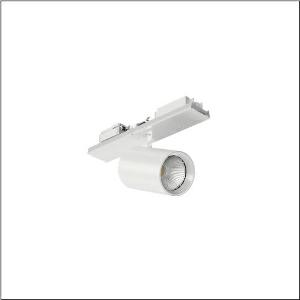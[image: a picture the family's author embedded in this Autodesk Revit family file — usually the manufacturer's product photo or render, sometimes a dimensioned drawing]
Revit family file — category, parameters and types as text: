
# Revit family: licross_r__spot_31_51sl147a43b_2678
name_source: partatom
category: Lighting Fixtures
units: mm (PartAtom-declared; Revit-internal decimal feet)

## family parameters
Cut with Voids When Loaded = No
Host = Face
Light Source = No
Part Type = Normal
Room Calculation Point = No
Round Connector Dimension = Use Diameter
Shared = No

## types (1)
- --- (1 x LED, 3720 lm, 27.9 W, 4000K)
    Apparent Load = 28 VA
    CIE Flux Codes = 93 97 100 100 100
    Color Rendering = 90
    Color Temperature = 4000K
    Default Elevation = 1800 mm
    Description = Licross® Spot 31, directional spotlight, light control with lens, of plastic, LED rated luminous flux: 3.720lm, light colour: 940, with plug, 3-pole, with phase selection, mains connection: 220..240V, AC, 50/60Hz, of aluminium, traffic white (RAL 9016), length: 300mm, diameter: 90mm, protection rating (complete): IP20, insulation class (complete): insulation class I (protective earthing), certification: CE, packaging unit: 1 piece
    Height = 175 mm
    Lamp = 1 x LED
    Lamp Light Flux = 3720 lm
    Lamp Power = 27.9 W
    Lamp count = 1
    Length = 90 mm
    Luminous efficacy = 133 lm/W
    Manufacturer = Siteco
    ModVariant = No
    Model = 51SL147A43B
    Mounting Place = Ceiling
    Mounting Type = Pendant
    Number of Poles = 1
    OnlyDefault = Yes
    Power Factor = 1
    Product Name = Licross® Spot 31
    Product group = directional spotlight
    ProductGroupID = 905
    Protection Class = Protection class I
    Protection Degree = IP 20
    RLX_Detail_Level = 1
    RLX_Emergency_Light_Flux = 0 lm
    RLX_Emergency_Type = 0
    RLX_Emergency_Type_DB = No
    RlxData = <blob elided: 14849 chars, md5=414b134d>
    Socket = socket
    Standby Power = 0 W
    System Light Flux = 3720 lm
    System Power = 28 W
    Type Comments = factory setting: luminous flux: 100 % | (ON | ON | ON) | 700 mA
    Type Image = l_1245720.jpg
    URL = http://relux.com
    VarID = @adj_102243
    Voltage = 0 V
    Weight = 0.00 kg
    Width = 0 mm  [stored 0 ft]

note: [stored X ft] marks values corroborated as IEEE doubles in the binary element streams (Revit-internal decimal feet)

## geometry (parser evidence)
native form markers: Sweep x11
no freeform markers — native parametric forms only
